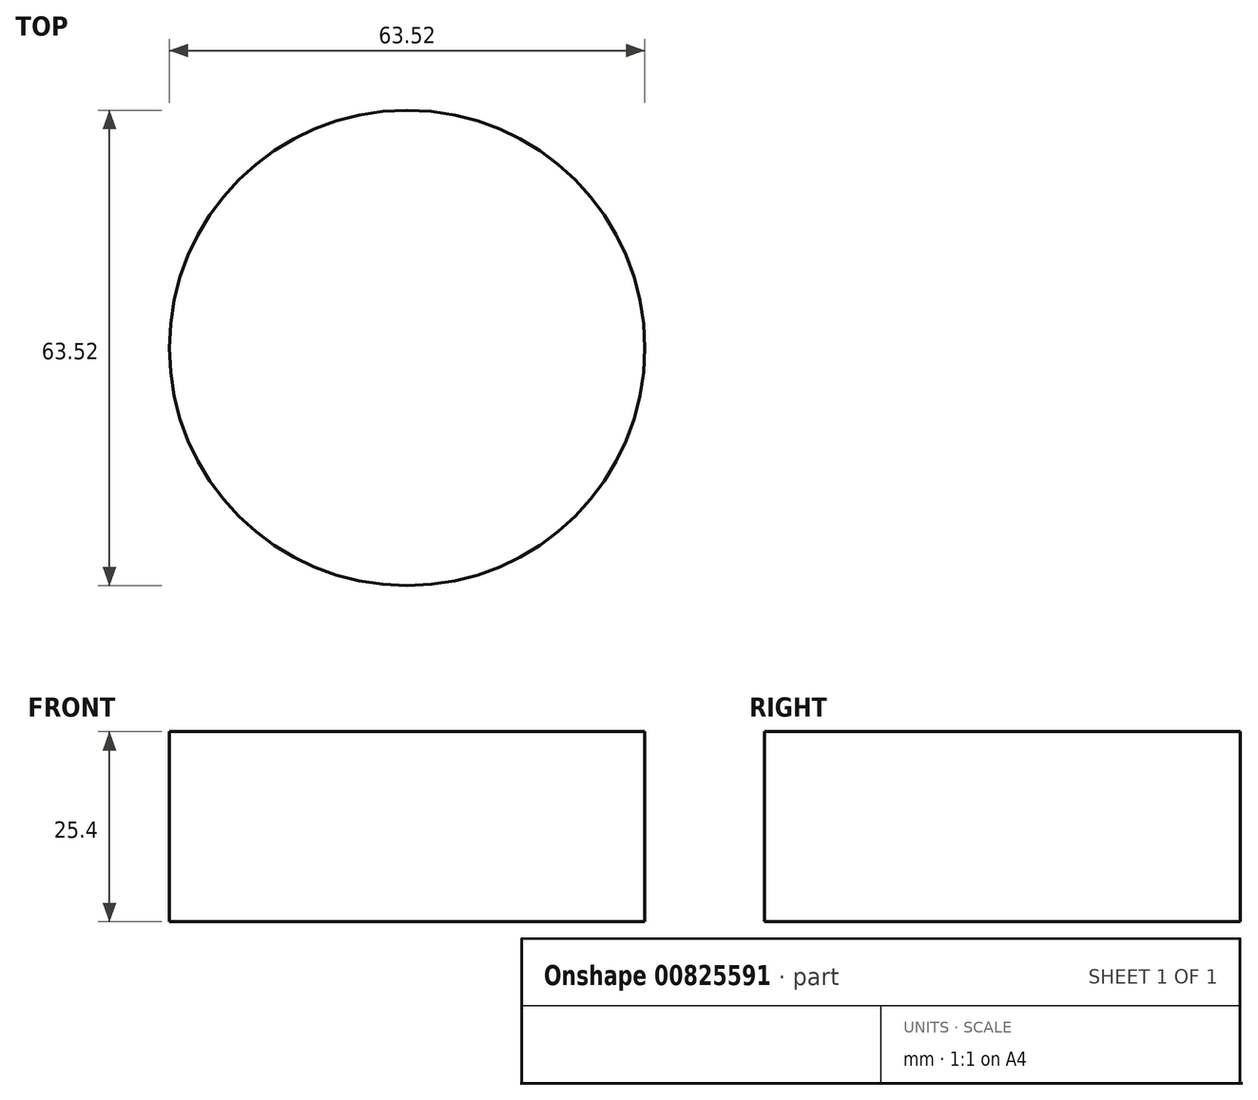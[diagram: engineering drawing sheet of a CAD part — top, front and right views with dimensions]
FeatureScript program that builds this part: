
annotation { "Feature Type Name" : "Feature", "Feature Type Description" : "" }
export const myFeature = defineFeature(function(context is Context, id is Id, definition is map)
    precondition{}
    {
        {
            var Q0;
            Q0=qCreatedBy(makeId("Top.planeOp"),FACE);
            var sketch = newSketch(context, id + "F0", { "sketchPlane" : qUnion([Q0])});
            skCircle(sketch, "E0", {"center": v(0, 0) * mm, "radius": 31.76 * mm});
            skSolve(sketch);
        }
        {
            var Q0;
            Q0=makeQuery(id+"F0.imprint","IMPRINT",FACE,{"disambiguationData":[TD([[makeQuery(id+"F0.imprint","IMPRINT",EDGE,{"derivedFrom":sQuery(id+"F0.wireOp",EDGE,"E0")}),1.0]])]});
            var sketch = newSketch(context, id + "F1", { "sketchPlane" : qUnion([Q0])});
            skSolve(sketch);
        }
        {
            var Q0;
            Q0=makeQuery(id+"F1.imprint","IMPRINT",FACE,{"disambiguationData":[TD([[makeQuery(id+"F1.imprint","IMPRINT",EDGE,{"derivedFrom":makeQuery(id+"F0.imprint","IMPRINT",EDGE,{"derivedFrom":sQuery(id+"F0.wireOp",EDGE,"E0")})}),1.0]])]});
            var sketch = newSketch(context, id + "F2", { "sketchPlane" : qUnion([Q0])});
            skSolve(sketch);
        }
        {
            var Q0;
            Q0=makeQuery(id+"F2.imprint","IMPRINT",FACE,{"disambiguationData":[TD([[makeQuery(id+"F2.imprint","IMPRINT",EDGE,{"derivedFrom":makeQuery(id+"F1.imprint","IMPRINT",EDGE,{"derivedFrom":makeQuery(id+"F0.imprint","IMPRINT",EDGE,{"derivedFrom":sQuery(id+"F0.wireOp",EDGE,"E0")})})}),1.0]])]});
            extrude(context, id + "F3", {"entities" : qUnion([Q0]), "depth" : 25.4 * mm, "offsetDistance" : 25.4 * mm});
        }
    });
